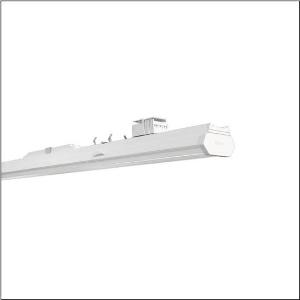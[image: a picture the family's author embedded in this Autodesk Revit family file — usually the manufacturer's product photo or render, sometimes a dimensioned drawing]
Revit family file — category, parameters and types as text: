
# Revit family: licross_11_protected_mo_51tp12mn4axg
name_source: partatom
category: Lighting Fixtures
units: mm (PartAtom-declared; Revit-internal decimal feet)

## family parameters
Cut with Voids When Loaded = No
Host = Face
Light Source = No
Part Type = Normal
Room Calculation Point = No
Round Connector Dimension = Use Diameter
Shared = No

## types (1)
- --- (1 x LED, 10020 lm, 55.3 W, 4000K)
    Apparent Load = 55 VA
    CIE Flux Codes = 73 92 98 99 100
    Color Rendering = 80
    Color Temperature = 4000K
    Default Elevation = 1800 mm
    Description = Licross 11 Protected MO, luminaire insert, of sheet steel, galvanised, coil coated, white, length: 1.500mm, width: 90mm, height: 101mm, LED rated luminous flux: 10.030lm, light colour: 840, SDCM (Standard Deviation of Colour Matching)MacAdam ≤ 2 SDCM (initial), control gear: ON/OFF Multilumen, with plug, 3-pole, with phase selection, mains connection: 220..240V, AC, 50/60Hz, rated input power: 55W, internal wiring halogen-free, primary light control with lens, of plastic, primary optical cover: cover, of PMMA, light emission: direct distribution, primary light characteristic: symmetric, protection rating (complete): IP64, insulation class (complete): insulation class I (protective earthing), certification: CE, ENEC, VDE, UKCA, protection symbol: D if used in an environment with conductive dust loads with corresponding accessories, impact resistance: IK06, permissible ambient temperature for indoor applications: -35..+40°C, corresponds to IFS (International Featured Standards) requirements for safety and quality in the food industry, reducing of maximum allowable ambient temperature of 5°C with ceiling mounting, LABS conformity tested according to VDMA 24364:2018-05, The light source and the operating device comply with the requirements of the Ecodesign Regulation (EU) 2019/2020 and are replaceable in accordance with this regulation, packaging unit: 1 piece
    Height = 92 mm
    Lamp = 1 x LED
    Lamp Light Flux = 10020 lm
    Lamp Power = 55.3 W
    Lamp count = 1
    Length = 1500 mm
    Luminous efficacy = 181 lm/W
    Manufacturer = Siteco
    ModVariant = No
    Model = 51TP12MN4AXG
    Mounting Place = Ceiling
    Mounting Type = Pendant
    Number of Poles = 1
    OnlyDefault = Yes
    Power Factor = 1
    Product Name = Licross 11 Protected MO
    Product group = luminaire insert | ceiling pendant
    ProductGroupID = 901
    Protection Class = Protection class I
    Protection Degree = IP 64
    RLX_Detail_Level = 1
    RLX_Emergency_Light_Flux = 0 lm
    RLX_Emergency_Type = 0
    RLX_Emergency_Type_DB = No
    RlxData = <blob elided: 22389 chars, md5=8b274908>
    Socket = socket
    Standby Power = 0 W
    System Light Flux = 10020 lm
    System Power = 55 W
    Type Comments = factory setting: luminous flux: 100 % | (A | C | E) | 126 mA
    Type Image = l_1256148.jpg
    URL = http://relux.com
    VarID = @adj_092011
    Voltage = 0 V
    Weight = 0.00 kg
    Width = 88 mm

## geometry (parser evidence)
native form markers: Blend x4, Sweep x13
no freeform markers — native parametric forms only
